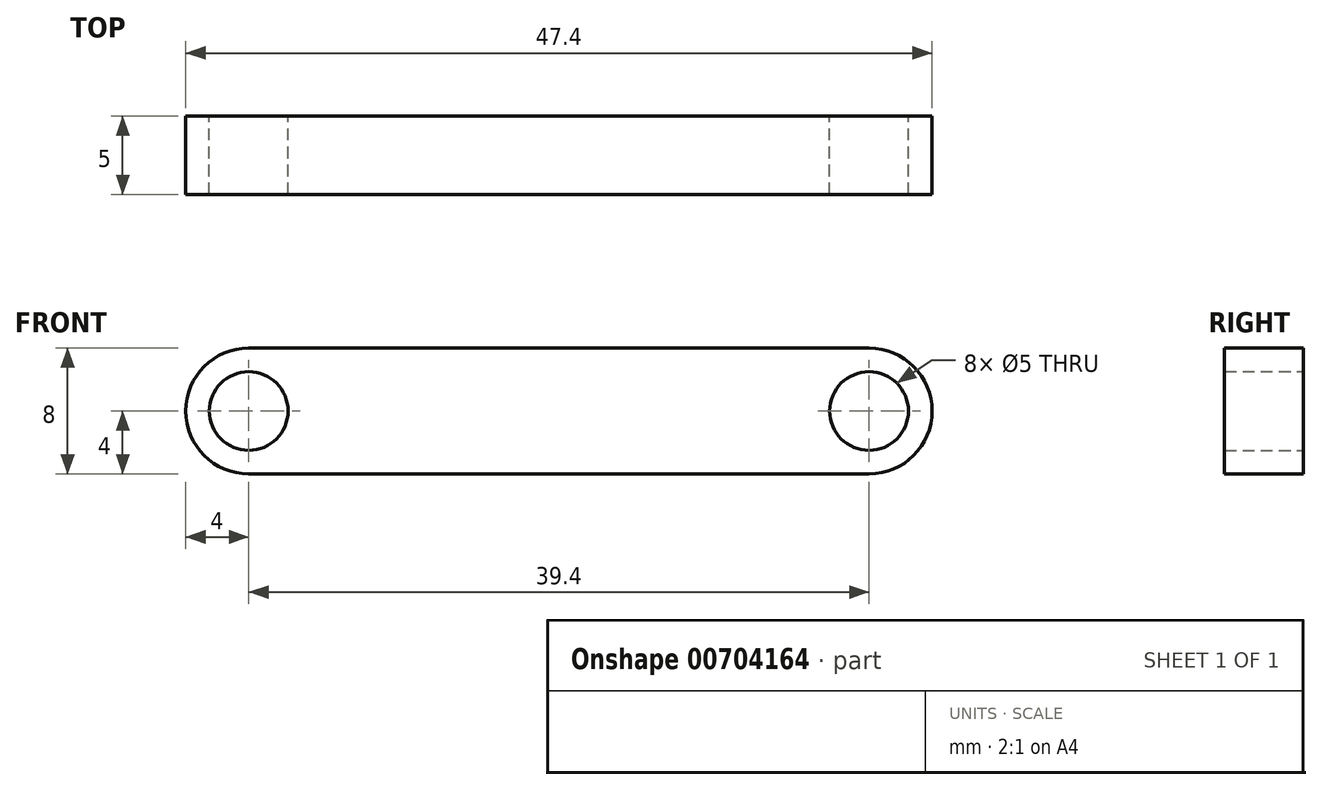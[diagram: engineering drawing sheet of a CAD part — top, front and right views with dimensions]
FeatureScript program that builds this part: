
annotation { "Feature Type Name" : "Feature", "Feature Type Description" : "" }
export const myFeature = defineFeature(function(context is Context, id is Id, definition is map)
    precondition{}
    {
        {
            var Q0;
            Q0=qCreatedBy(makeId("Front.planeOp"),FACE);
            var sketch = newSketch(context, id + "F0", { "sketchPlane" : qUnion([Q0])});
            skLineSegment(sketch, "E0.bottom", {"start": v(-19.7, 4) * mm, "end": v(0, 4) * mm});
            skLineSegment(sketch, "E0.top", {"start": v(-19.7, -4) * mm, "end": v(0, -4) * mm});
            skLineSegment(sketch, "E0.left", {"start": v(-19.7, 4) * mm, "end": v(-19.7, -4) * mm, "construction": true});
            skLineSegment(sketch, "E0.right", {"start": v(0, 4) * mm, "end": v(0, -4) * mm});
            skArc(sketch, "E1", {"start": v(-19.7, -4) * mm, "mid": v(-23.7, 0) * mm, "end": v(-19.7, 4) * mm});
            skCircle(sketch, "E2", {"center": v(-19.7, 0) * mm, "radius": 2.5 * mm});
            skLineSegment(sketch, "E3.MirrorCS", {"start": v(19.7, -4) * mm, "end": v(0, -4) * mm});
            skArc(sketch, "E4.MirrorCS", {"start": v(19.7, -4) * mm, "mid": v(23.7, 0) * mm, "end": v(19.7, 4) * mm});
            skCircle(sketch, "E5.MirrorC", {"center": v(19.7, 0) * mm, "radius": 2.5 * mm});
            skLineSegment(sketch, "E6.MirrorCS", {"start": v(19.7, 4) * mm, "end": v(0, 4) * mm});
            skSolve(sketch);
        }
        {
            var Q0;
            Q0=makeQuery(id+"F0.imprint","IMPRINT",FACE,{"disambiguationData":[TD([[makeQuery(id+"F0.imprint","IMPRINT",EDGE,{"derivedFrom":sQuery(id+"F0.wireOp",EDGE,"E0.bottom")}),-1.0]])]});
            var Q1;
            Q1=makeQuery(id+"F0.imprint","IMPRINT",FACE,{"disambiguationData":[TD([[makeQuery(id+"F0.imprint","IMPRINT",EDGE,{"derivedFrom":sQuery(id+"F0.wireOp",EDGE,"E0.right")}),1.0]])]});
            extrude(context, id + "F1", {"entities" : qUnion([Q0, Q1]), "depth" : 5 * mm, "offsetDistance" : 25 * mm});
        }
    });
